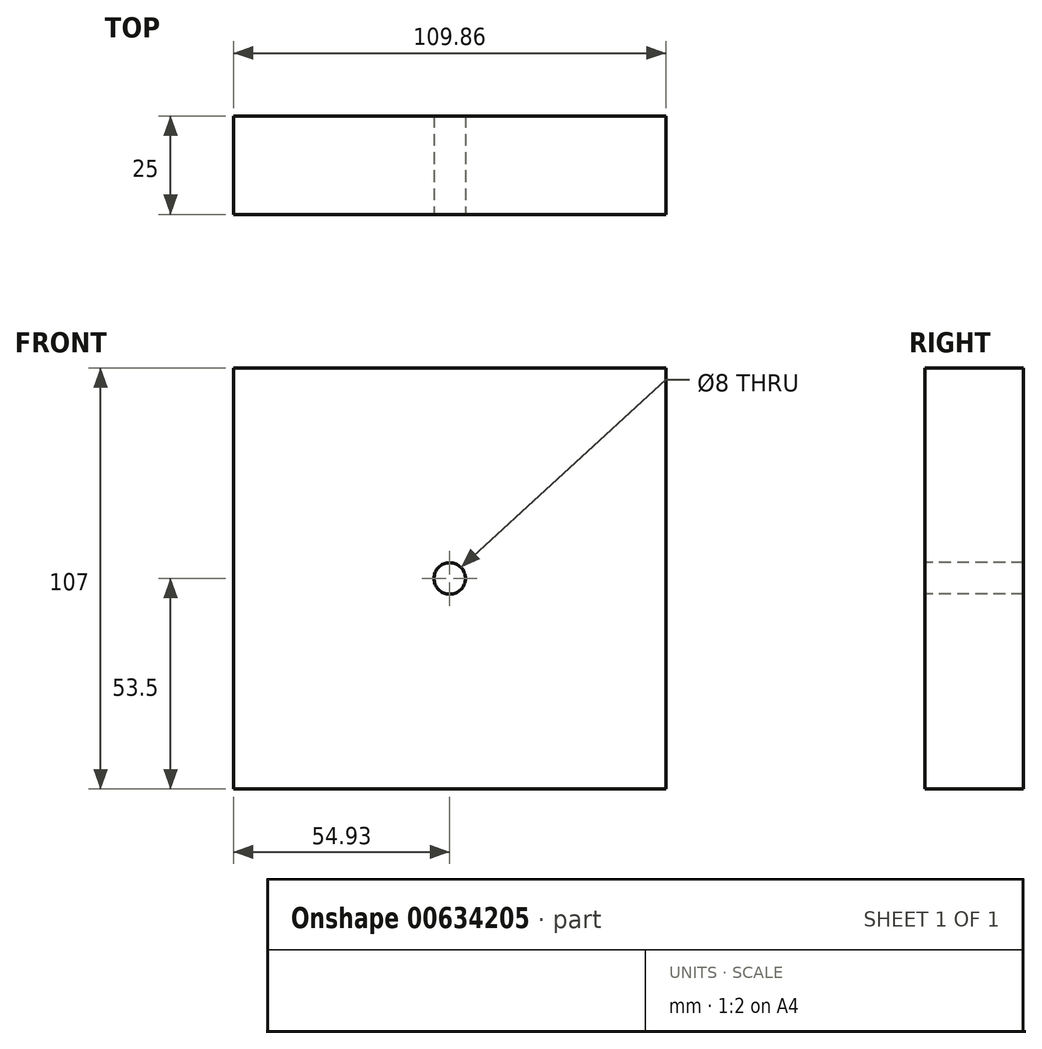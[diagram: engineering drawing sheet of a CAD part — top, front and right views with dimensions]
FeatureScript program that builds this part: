
annotation { "Feature Type Name" : "Feature", "Feature Type Description" : "" }
export const myFeature = defineFeature(function(context is Context, id is Id, definition is map)
    precondition{}
    {
        {
            var Q0;
            Q0=qCreatedBy(makeId("Front.planeOp"),FACE);
            var sketch = newSketch(context, id + "F0", { "sketchPlane" : qUnion([Q0])});
            skLineSegment(sketch, "E0.bottom", {"start": v(54.93, 53.5) * mm, "end": v(-54.93, 53.5) * mm});
            skLineSegment(sketch, "E0.top", {"start": v(54.93, -53.5) * mm, "end": v(-54.93, -53.5) * mm});
            skLineSegment(sketch, "E0.left", {"start": v(54.93, 53.5) * mm, "end": v(54.93, -53.5) * mm});
            skLineSegment(sketch, "E0.right", {"start": v(-54.93, 53.5) * mm, "end": v(-54.93, -53.5) * mm});
            skPoint(sketch, "E0.middle", {"position": v(0, 0) * mm});
            skSolve(sketch);
        }
        {
            var Q0;
            Q0 = qSketchRegion(id + "F0", true);
            extrude(context, id + "F1", {"entities" : qUnion([Q0]), "depth" : 25 * mm, "offsetDistance" : 25 * mm});
        }
        {
            var Q0;
            Q0=makeQuery(id+"F1.opExtrude","CAP_FACE",FACE,{"disambiguationData":[OSD([sQuery(id+"F0.wireOp",EDGE,"E0.bottom"),sQuery(id+"F0.wireOp",EDGE,"E0.top"),sQuery(id+"F0.wireOp",EDGE,"E0.left"),sQuery(id+"F0.wireOp",EDGE,"E0.right")])],"isStart":false});
            var sketch = newSketch(context, id + "F2", { "sketchPlane" : qUnion([Q0])});
            skPoint(sketch, "E1", {"position": v(0, 0) * mm});
            skSolve(sketch);
        }
        {
            var Q0;
            Q0=sQuery(id+"F2.wireOp",VERTEX,"E1");
            var Q1;
            Q1=makeQuery(id+"F1.opExtrude","SWEPT_BODY",BODY,{"disambiguationData":[OSD([sQuery(id+"F0.wireOp",EDGE,"E0.bottom"),sQuery(id+"F0.wireOp",EDGE,"E0.top"),sQuery(id+"F0.wireOp",EDGE,"E0.left"),sQuery(id+"F0.wireOp",EDGE,"E0.right")])]});
            hole(context, id + "F3", {"style" : HoleStyle.SIMPLE, "endStyle" : HoleEndStyle.THROUGH, "holeDiameter" : 8 * mm, "majorDiameter" : 5 * mm, "isTappedThrough" : true, "tappedDepth" : 12 * mm, "tapClearance" : 3, "locations" : qUnion([Q0]), "scope" : qUnion([Q1])});
        }
    });
